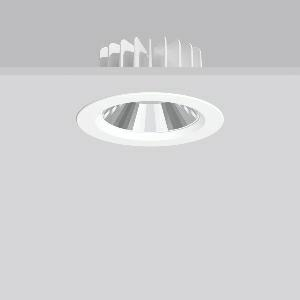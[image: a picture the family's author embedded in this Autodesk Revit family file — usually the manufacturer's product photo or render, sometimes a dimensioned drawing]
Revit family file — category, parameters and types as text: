
# Revit family: ledona_round_ip20_901795_002_1_76_30fa
name_source: partatom
category: Lighting Fixtures
units: mm (PartAtom-declared; Revit-internal decimal feet)

## family parameters
Cut with Voids When Loaded = No
Host = Face
Light Source = No
Part Type = Normal
Room Calculation Point = No
Round Connector Dimension = Use Diameter
Shared = No

## types (1)
- MultiLumen 1 (1 x LED Modul 940, 1700 lm, 4000)
    Apparent Load = 12 VA
    Approval mark = CE
    CIE Flux Codes = 91 100 100 100 100
    Color Rendering = 92
    Color Temperature = 4000
    Default Elevation = 1800 mm
    Description = Series: LEDONA round
Recessed LED downlight featuring advanced technology and sophisticated design. Housing: die-cast aluminium constructed as heat sink.Bezel ring: die-cast aluminium, powder-coated. Open version. Highly polished four-segment faceted aluminium reflector with light mixing chamber. MultiLumen: Luminous flux adjustable in different steps. Best colour rendering index Ra>90. Installation without tools thanks to spring fastening system. Connected converter included in separate gearbox. With connecting cable (L 250 mm). Suitable for through wiring as standard. 
Colour: white
Diameter: 180 mm
Height: 3 mm
Cut-out diameter: 160 mm
Recess height: 89 mm
Luminaire: recess height: 89 mm
Lamp: LED
Socket: without socket
Colour temperature: 4000K
Colour rendering index (CRI): 92
System power: 12 W
Rated luminous flux: 1700 lm
Beam angle Down: 64°
Luminous efficiency: 142 lm/W
System power 2: 19 W
Rated luminous flux 2: 2750 lm
Luminous efficiency 2: 145 lm/W
System power 3: 27 W
Rated luminous flux 3: 3700 lm
Luminous efficiency 3: 137 lm/W
System power 4: 39 W
Rated luminous flux 4: 4950 lm
Luminous efficiency 4: 127 lm/W
Control gear: Converter, dimmable, DALI
Protection class: II
Type of protection: IP 20
    Height = 0 mm  [stored 0 ft]
    Lamp = 1 x LED Modul 940
    Lamp Light Flux = 1700 lm
    Lamp count = 1
    Length = 180 mm  [stored 0.590551 ft]
    Lifetime = 50000 h
    Luminous efficacy = 142 lm/W
    Manufacturer = RZB
    ModVariant = No
    Model = 901795.002.1.76
    Mounting Place = Ceiling
    Mounting Type = Recessed
    Number of Poles = 1
    OnlyDefault = Yes
    Power Factor = 1
    Product Name = LEDONA round IP20
    Product group = Recessed downlights
    ProductGroupID = 402
    Protection Class = Protection class II
    Protection Degree = IP 20
    RLX_Detail_Level = 1
    RLX_Emergency_Light_Flux = 0 lm
    RLX_Emergency_Type = 0
    RLX_Emergency_Type_DB = No
    RlxData = <blob elided: 38329 chars, md5=7bd8c7b0>
    Socket = socket
    Standby Power = 0 W
    System Light Flux = 1700 lm
    System Power = 12 W
    Type Comments = MultiLumen 1
    Type Image = 901385.002.jpg
    URL = http://relux.com
    VarID = multilumen_1
    Voltage = 230 V
    Voltage Range = 220-240 V
    Weight = 0.00 kg
    Width = 0 mm  [stored 0 ft]

note: [stored X ft] marks values corroborated as IEEE doubles in the binary element streams (Revit-internal decimal feet)

## geometry (parser evidence)
native form markers: Blend x4, Sweep x8
no freeform markers — native parametric forms only
